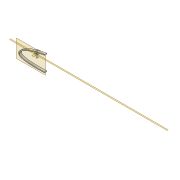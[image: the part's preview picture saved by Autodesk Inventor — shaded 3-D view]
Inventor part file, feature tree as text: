
AUTODESK INVENTOR PART (.ipt)
format: ipt  version: 2022 (Build 260153000, 153)  size: 696,832 bytes
history: native  units: mm
features: extrude x10, sketch x10, projected_geometry x7, plane x4, shell x1, fillet x1, mirror x1
ambient origin geometry x8: Origin, YZ Plane, XZ Plane, XY Plane, X Axis, Y Axis, Z Axis, Center Point
bodies: Solid1 (feature_tree)
feature tree (34):
  extrude  "Extrusion1"  Depth=3.0mm
  shell  "Shell1"  Thickness=5.215mm
  plane  "Work Plane3"
  sketch  "Sketch26"  dims[d69=4.1mm d70=63.6mm]
  plane  "Work Plane4"
  extrude  "Extrusion9"  Depth=63.6mm
  plane  "Work Plane5"
  extrude  "Extrusion10"  Depth=4.2mm
  extrude  "Extrusion11"  Depth=6.0mm
  extrude  "Extrusion12"  Depth=21.0mm TaperAngle=0.0deg
  plane  "Work Plane6"
  extrude  "Extrusion13"  Depth=5.0mm
  extrude  "Extrusion15"  Depth=3.0mm TaperAngle=0.0deg
  extrude  "Extrusion16"  Depth=2.0mm
  extrude  "Extrusion17"  Depth=4.0mm
  fillet  "Fillet2"  Radius=4.0mm
  extrude  "Extrusion18"  Depth=95.0mm
  mirror  "Mirror1"
  sketch  "Sketch3"  dims[d0=12.0mm d1=0.0mm d2=3.0mm d68=5.215mm]
  sketch  "Sketch27"  dims[d71=12.0mm d72=4.2mm]
  projected_geometry  "Projected Loop13"
  sketch  "Sketch29"  dims[d73=63.6mm d74=6.0mm]
  sketch  "Sketch30"  dims[d75=7.0mm d76=21.0mm d77=0.0mm]
  projected_geometry  "Projected Loop14"
  sketch  "Sketch31"  dims[d78=-11.5mm d79=5.0mm]
  projected_geometry  "Projected Loop15"
  projected_geometry  "Projected Loop16"
  projected_geometry  "Projected Loop17"
  sketch  "Sketch33"  dims[d80=10.0mm d83=3.0mm d84=0.0mm]
  sketch  "Sketch34"  dims[d86=0.65mm d87=2.0mm]
  projected_geometry  "Projected Loop18"
  sketch  "Sketch35"  dims[d88=2.0mm d89=4.0mm d90=4.0mm]
  projected_geometry  "Projected Loop19"
  sketch  "Sketch36"  dims[d91=3.0mm d92=0.0mm d93=12.0mm d94=7.0mm d95=0.0mm d96=28.0mm d98=9.0mm d99=0.0mm d103=200.0mm d104=100.0mm d105=0.0mm d106=7.0mm d107=4.1mm d108=7.0mm d109=2.0mm d110=0.0mm d111=2.0mm d112=0.0mm d113=2.0mm d114=95.0mm d115=10.0mm d116=0.0mm]
